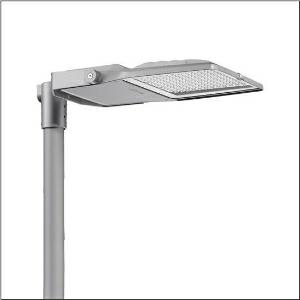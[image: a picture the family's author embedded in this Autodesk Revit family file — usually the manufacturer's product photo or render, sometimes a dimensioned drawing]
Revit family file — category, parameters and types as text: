
# Revit family: floodlight_fl_21_iq_midi___pl43_5xa7781f2a3a_7a49
name_source: partatom
category: Lighting Fixtures
units: mm (PartAtom-declared; Revit-internal decimal feet)

## family parameters
Cut with Voids When Loaded = No
Host = Face
Light Source = No
Part Type = Normal
Room Calculation Point = No
Round Connector Dimension = Use Diameter
Shared = No

## types (1)
- --- (1 x LED, 36680 lm, 270.2 W, 3000K)
    Apparent Load = 270 VA
    CIE Flux Codes = 27 78 99 100 100
    Color Rendering = 70
    Color Temperature = 3000K
    Default Elevation = 1800 mm
    Description = Floodlight FL 21 iQ midi, floodlight, primary light control with lens, of PMMA, primary optical cover: protective disc, of toughened safety glass, transparent, light distribution: PL43, light emission: direct distribution, installation type: surface-mounted, LED, High Power LED, rated luminous flux: 36.680lm, luminous efficacy: 136lm/W, light colour: 730, colour temperature: 3000K, control gear: iQ Comfort/DALI, control: optimised constant luminous flux control (CLO 2.0), Desk-Remote (wireless, voltage-free reading and setting of iQ features in the workshop via application-optimized NFC function/RFID function), Light-Fading, Smart-Wire, Night-Set, Lumen-Switch, Temp-Guard, Auto-Match, with terminal, 6-pole, mains connection: 220..240V, AC, 50/60Hz, start of lifetime: 270W, end of service life: 287W, reduction: 117W, luminaire housing, of diecast aluminium, powder-coated, Siteco® metallic grey (DB 702S), corrosivity category C5 mid according to DIN EN ISO 12944, suitable for swimming pools, chlorine-resistant, sealing non-destructively replaceable, please order mast flange separately, mast bracket, of steel, galvanised, powder-coated, Siteco® metallic grey (DB 702S), protection rating (complete): IP66, insulation class (complete): insulation class II (safety insulation), certification: CE, ENEC, VDE, protection symbol: D, impact resistance: IK08, permissible operating ambient temperature: -40..+40°C, permissible operating ambient temperature for outdoor applications: -40..+50°C, standard: DIN EN 12944, LABS conformity tested according to VDMA 24364:2018-05, packaging unit: 1 piece

Light Distribution: PL43
    Height = 76 mm
    Lamp = 1 x LED
    Lamp Light Flux = 36680 lm
    Lamp Power = 270.2 W
    Lamp count = 1
    Length = 657 mm
    Luminous efficacy = 136 lm/W
    Manufacturer = Siteco
    ModVariant = No
    Model = 5XA7781F2A3A
    Number of Poles = 1
    OnlyDefault = Yes
    Power Factor = 1
    Product Name = Floodlight FL 21 iQ midi | PL43
    Product group = floodlight | pylon annexe
    ProductGroupID = 6201
    Protection Class = Protection class II
    Protection Degree = IP 66
    RLX_Detail_Level = 1
    RLX_Emergency_Light_Flux = 0 lm
    RLX_Emergency_Type = 0
    RLX_Emergency_Type_DB = No
    RlxData = <blob elided: 153489 chars, md5=b8664699>
    Socket = socket
    Standby Power = 0 W
    System Light Flux = 36680 lm
    System Power = 270 W
    Type Comments = factory setting: luminous flux: 100 % | dim-lin: 254 | 620 mA
    Type Image = l_1007123.jpg
    URL = http://relux.com
    VarID = @adj_126321
    Voltage = 0 V
    Weight = 0.00 kg
    Width = 442 mm

## geometry (parser evidence)
native form markers: Blend x4, Sweep x14
no freeform markers — native parametric forms only
